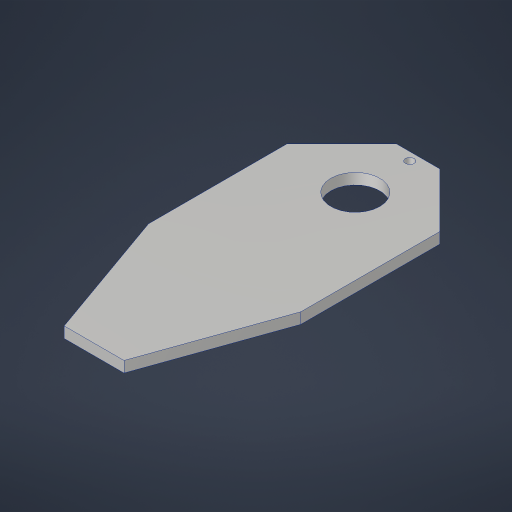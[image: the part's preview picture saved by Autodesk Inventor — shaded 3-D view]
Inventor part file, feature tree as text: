
AUTODESK INVENTOR PART (.ipt)
format: ipt  version: 2023.4 (Build 274418000, 418)  size: 198,656 bytes
history: native  units: in
note: dims shown in document units (in); Inventor stores cm internally (conversion verified against a paired STEP export)
features: sketch x2, extrude x2, hole x1, projected_geometry x1
ambient origin geometry x8: Origin, YZ Plane, XZ Plane, XY Plane, X Axis, Y Axis, Z Axis, Center Point
bodies: Solid1 (feature_tree)
feature tree (6):
  sketch  "Sketch1"  dims[d0=2.0in d1=1.0in]
  extrude  "Extrusion1"  Depth=1.0in
  hole  "Hole1"  [1 undecoded]
  extrude  "Extrusion2"  Depth=0.25in
  sketch  "Sketch2"  dims[d2=3.5in d4=1.125in d5=0.375in d6=1.25in d7=6.0in d8=0.25in d9=0.0in d11=0.201in d12=0.75in d13=0.385in d14=0.25in d15=0.5635in d16=1.0in d17=0.8108in d18=1.0in d19=1.25in d20=1.25in d21=1.0in d22=2.0in d23=1.375in d24=3.0in d25=0.0in d26=0.0in]
  projected_geometry  "Project Cut Edges1"
note: 1 required parameter value undecoded (feature->parameter linkage not recoverable at this tier; creation-order binding heuristic only, values carry confidence <= 0.55)
